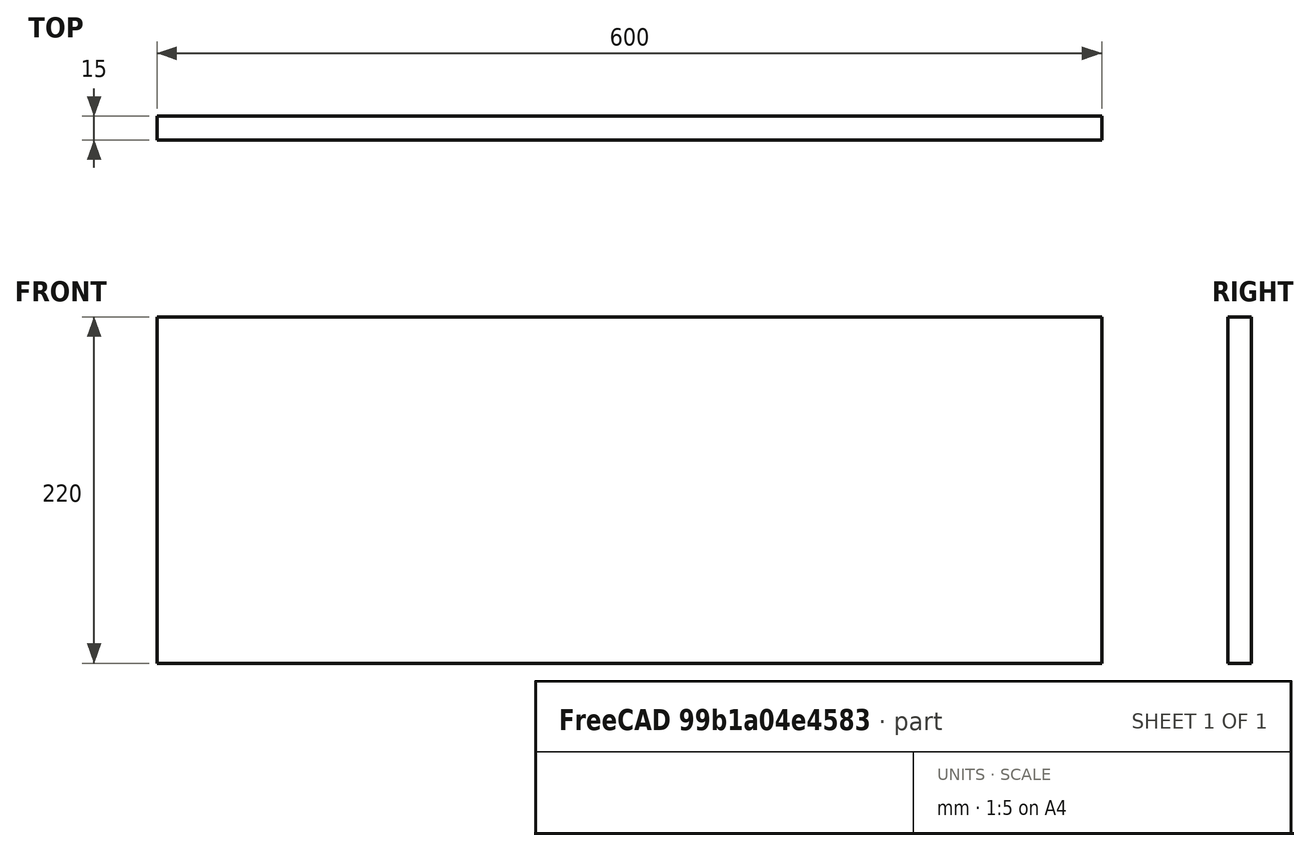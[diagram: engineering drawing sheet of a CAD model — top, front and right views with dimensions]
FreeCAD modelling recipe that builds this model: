
FCSTD DOCUMENT  (FreeCAD 1.0R39319 (Git))
Label: internal_plate
License: All rights reserved
LicenseURL: https://en.wikipedia.org/wiki/All_rights_reserved
objects: Sketcher::SketchObject×1, PartDesign::Pad×1, PartDesign::Body×1
note: 6 computed .brp shape members not serialized (recipe doc carries the construction recipe); baked Part::Feature solids carry a one-line shape summary decoded from their .brp

FEATURE [Sketcher::SketchObject] Sketch  label="internal_plate_s"
  ArcFitTolerance = 1e-06
  AttachmentSupport = -> [XZ_Plane]
  FullyConstrained = true
  MakeInternals = false
  MapMode = 5
  Placement = pos=(0,0,0) rot=(1,0,0;1.5708rad)
  sketch-geometry (4):
    g0: LineSegment StartX=0 StartY=0 StartZ=0 EndX=600 EndY=0 EndZ=0
    g1: LineSegment StartX=600 StartY=0 StartZ=0 EndX=600 EndY=220 EndZ=0
    g2: LineSegment StartX=600 StartY=220 StartZ=0 EndX=0 EndY=220 EndZ=0
    g3: LineSegment StartX=0 StartY=220 StartZ=0 EndX=0 EndY=0 EndZ=0
  constraints (11):
    c: Coincident(g0,g1)
    c: Coincident(g1,g2)
    c: Coincident(g2,g3)
    c: Coincident(g3,g0)
    c: Horizontal(g0)
    c: Horizontal(g2)
    c: Vertical(g1)
    c: Vertical(g3)
    c: Coincident(g0,g-1)
    c: DistanceX(g2,g2) = 600
    c: DistanceY(g3,g3) = 220
FEATURE [PartDesign::Pad] Pad  label="internal_plate"
  Direction = (0,-1,2e-16)
  Length = 15
  Length2 = 10
  Placement = pos=(0,0,0) rot=(1,0,0;1.5708rad)
  Profile = -> Sketch
  ReferenceAxis = -> Sketch [N_Axis]
  Refine = true
  Suppressed = false
  Type = 0
FEATURE [PartDesign::Body] Body  label="internal_plate_body"
  AllowCompound = false
  Group = -> [Sketch,Pad]
  Origin = -> Origin
  Tip = -> Pad
